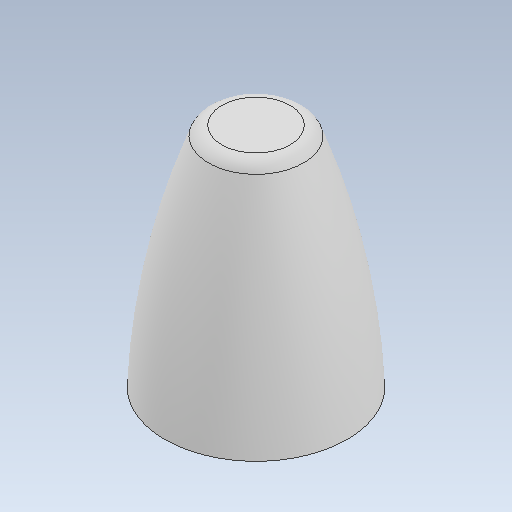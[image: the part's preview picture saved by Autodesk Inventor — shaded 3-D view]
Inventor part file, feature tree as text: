
AUTODESK INVENTOR PART (.ipt)
format: ipt  version: 2020 (Build 240168000, 168)  size: 169,984 bytes
history: native  units: in
note: dims shown in document units (in); Inventor stores cm internally (conversion verified against a paired STEP export)
features: fillet x1
ambient origin geometry x8: Origin, YZ Plane, XZ Plane, XY Plane, X Axis, Y Axis, Z Axis, Center Point
bodies: Solid1 (feature_tree)
feature tree (1):
  fillet  "Fillet3"  [1 undecoded]
note: 1 required parameter value undecoded (feature->parameter linkage not recoverable at this tier; creation-order binding heuristic only, values carry confidence <= 0.55)
